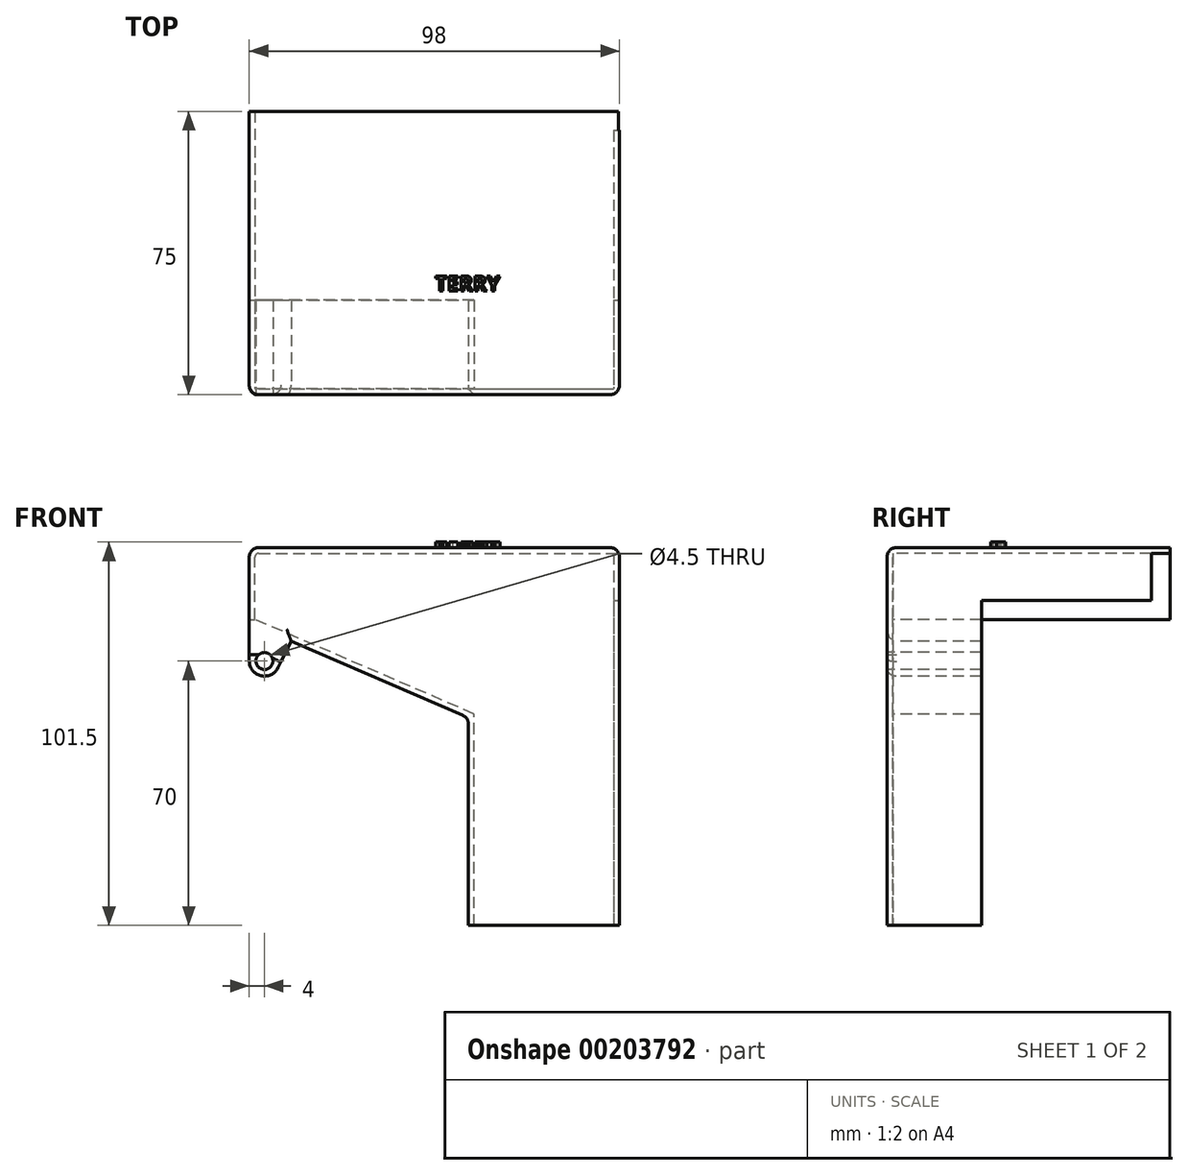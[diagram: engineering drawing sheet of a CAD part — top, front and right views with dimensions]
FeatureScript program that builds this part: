
annotation { "Feature Type Name" : "Feature", "Feature Type Description" : "" }
export const myFeature = defineFeature(function(context is Context, id is Id, definition is map)
    precondition{}
    {
        {
            var Q0;
            Q0=qCreatedBy(makeId("Front.planeOp"),FACE);
            var sketch = newSketch(context, id + "F0", { "sketchPlane" : qUnion([Q0])});
            skLineSegment(sketch, "E0", {"start": v(0, 0) * mm, "end": v(0, -55) * mm});
            skLineSegment(sketch, "E1", {"start": v(0, -55) * mm, "end": v(40, -55) * mm});
            skLineSegment(sketch, "E2", {"start": v(40, -55) * mm, "end": v(40, 45) * mm});
            skLineSegment(sketch, "E3", {"start": v(40, 45) * mm, "end": v(-58, 45) * mm});
            skLineSegment(sketch, "E4", {"start": v(-58, 45) * mm, "end": v(-58, 25) * mm});
            skLineSegment(sketch, "E5", {"start": v(-58, 25) * mm, "end": v(0, 0) * mm});
            skSolve(sketch);
        }
        {
            var Q0;
            Q0=makeQuery(id+"F0.imprint","IMPRINT",FACE,{"disambiguationData":[TD([[makeQuery(id+"F0.imprint","IMPRINT",EDGE,{"derivedFrom":sQuery(id+"F0.wireOp",EDGE,"E0")}),1.0]])]});
            extrude(context, id + "F1", {"entities" : qUnion([Q0]), "oppositeDirection" : true, "depth" : 1.5 * mm});
        }
        {
            var Q0;
            Q0=makeQuery(id+"F1.opExtrude","CAP_FACE",FACE,{"disambiguationData":[OSD([sQuery(id+"F0.wireOp",EDGE,"E0"),sQuery(id+"F0.wireOp",EDGE,"E1"),sQuery(id+"F0.wireOp",EDGE,"E2"),sQuery(id+"F0.wireOp",EDGE,"E3"),sQuery(id+"F0.wireOp",EDGE,"E4"),sQuery(id+"F0.wireOp",EDGE,"E5")])],"isStart":true});
            var sketch = newSketch(context, id + "F2", { "sketchPlane" : qUnion([Q0])});
            skLineSegment(sketch, "E6", {"start": v(-58, 25) * mm, "end": v(-58, 7.07) * mm, "construction": true});
            skLineSegment(sketch, "E7", {"start": v(-58, 25) * mm, "end": v(0, 0) * mm, "construction": true});
            skLineSegment(sketch, "E8.0", {"start": v(-54, 25) * mm, "end": v(-54, 7.07) * mm});
            skCircle(sketch, "E9", {"center": v(-54, 15) * mm, "radius": 2.25 * mm});
            skArc(sketch, "E10", {"start": v(-54, 19) * mm, "mid": v(-54.36, 18.98) * mm, "end": v(-54.71, 18.94) * mm});
            skLineSegment(sketch, "E11", {"start": v(-58, 15) * mm, "end": v(-58, 25) * mm});
            skLineSegment(sketch, "E12", {"start": v(-50.42, 13.21) * mm, "end": v(-46.92, 20.22) * mm});
            skLineSegment(sketch, "E13", {"start": v(-46.92, 20.22) * mm, "end": v(-58, 25) * mm});
            skArc(sketch, "E14.trimOffspring", {"start": v(-58, 15) * mm, "mid": v(-54.92, 11.1) * mm, "end": v(-50.42, 13.21) * mm});
            skSolve(sketch);
        }
        {
            var Q0;
            {var subQ10=sQuery(id+"F2.wireOp",EDGE,"E12");Q0=makeQuery(id+"F2.imprint","IMPRINT",FACE,{"disambiguationData":[TD([[makeQuery(id+"F2.imprint","IMPRINT",EDGE,{"derivedFrom":subQ10}),1.0]])]});}
            var Q1;
            {var subQ0=sQuery(id+"F2.wireOp",EDGE,"E14.trimOffspring");Q1=makeQuery(id+"F2.imprint","IMPRINT",FACE,{"disambiguationData":[TD([[makeQuery(id+"F2.imprint","IMPRINT",EDGE,{"derivedFrom":subQ0}),1.0]])]});}
            extrude(context, id + "F3", {"entities" : qUnion([Q0, Q1]), "operationType" : NewBodyOperationType.ADD, "oppositeDirection" : true, "depth" : 25 * mm});
        }
        {
            var Q0;
            Q0=makeQuery(id+"F1.opExtrude","CAP_FACE",FACE,{"disambiguationData":[OSD([sQuery(id+"F0.wireOp",EDGE,"E0"),sQuery(id+"F0.wireOp",EDGE,"E1"),sQuery(id+"F0.wireOp",EDGE,"E2"),sQuery(id+"F0.wireOp",EDGE,"E3"),sQuery(id+"F0.wireOp",EDGE,"E4"),sQuery(id+"F0.wireOp",EDGE,"E5")])],"isStart":false});
            var sketch = newSketch(context, id + "F4", { "sketchPlane" : qUnion([Q0])});
            skLineSegment(sketch, "E15", {"start": v(0, -55) * mm, "end": v(0, 0) * mm});
            skLineSegment(sketch, "E16", {"start": v(0, 0) * mm, "end": v(58, 25) * mm});
            skLineSegment(sketch, "E17", {"start": v(58, 25) * mm, "end": v(58, 45) * mm});
            skLineSegment(sketch, "E18", {"start": v(58, 45) * mm, "end": v(-40, 45) * mm});
            skLineSegment(sketch, "E19", {"start": v(-40, 45) * mm, "end": v(-40, -55) * mm});
            skLineSegment(sketch, "E20.0", {"start": v(-38.5, 43.5) * mm, "end": v(-38.5, -55) * mm});
            skLineSegment(sketch, "E20.1", {"start": v(-1.5, -55) * mm, "end": v(-1.5, 0.99) * mm});
            skLineSegment(sketch, "E20.2", {"start": v(-1.5, 0.99) * mm, "end": v(56.5, 25.99) * mm});
            skLineSegment(sketch, "E20.3", {"start": v(56.5, 25.99) * mm, "end": v(56.5, 43.5) * mm});
            skLineSegment(sketch, "E20.4", {"start": v(56.5, 43.5) * mm, "end": v(-38.5, 43.5) * mm});
            skSolve(sketch);
        }
        {
            var Q0;
            {var subQ2=sQuery(id+"F4.wireOp",EDGE,"E15");Q0=makeQuery(id+"F4.imprint","IMPRINT",FACE,{"disambiguationData":[TD([[makeQuery(id+"F4.imprint","IMPRINT",EDGE,{"derivedFrom":subQ2}),-1.0]])]});}
            extrude(context, id + "F5", {"entities" : qUnion([Q0]), "operationType" : NewBodyOperationType.ADD, "depth" : 23.5 * mm});
        }
        {
            var Q0;
            Q0=makeQuery(id+"F5.boolean.opBoolean","MERGE",FACE,{"derivedFrom":[makeQuery(id+"F3.opExtrude","CAP_FACE",FACE,{"disambiguationData":[OSD([sQuery(id+"F2.wireOp",EDGE,"E9"),sQuery(id+"F2.wireOp",EDGE,"E11"),sQuery(id+"F2.wireOp",EDGE,"E12"),sQuery(id+"F2.wireOp",EDGE,"E13"),sQuery(id+"F2.wireOp",EDGE,"E14.trimOffspring")])],"isStart":false}),makeQuery(id+"F5.opExtrude","CAP_FACE",FACE,{"disambiguationData":[OSD([sQuery(id+"F0.wireOp",EDGE,"E1"),sQuery(id+"F4.wireOp",EDGE,"E15"),sQuery(id+"F4.wireOp",EDGE,"E16"),sQuery(id+"F4.wireOp",EDGE,"E17"),sQuery(id+"F4.wireOp",EDGE,"E18"),sQuery(id+"F4.wireOp",EDGE,"E19"),sQuery(id+"F4.wireOp",EDGE,"E20.0"),sQuery(id+"F4.wireOp",EDGE,"E20.1"),sQuery(id+"F4.wireOp",EDGE,"E20.2"),sQuery(id+"F4.wireOp",EDGE,"E20.3"),sQuery(id+"F4.wireOp",EDGE,"E20.4")])],"isStart":false})]});
            var sketch = newSketch(context, id + "F6", { "sketchPlane" : qUnion([Q0])});
            skLineSegment(sketch, "E21", {"start": v(56.5, 25.99) * mm, "end": v(56.5, 43.5) * mm});
            skLineSegment(sketch, "E22", {"start": v(56.5, 43.5) * mm, "end": v(-40, 43.5) * mm});
            skLineSegment(sketch, "E23", {"start": v(-40, 43.5) * mm, "end": v(-40, 45) * mm});
            skLineSegment(sketch, "E24", {"start": v(-40, 45) * mm, "end": v(58, 45) * mm});
            skLineSegment(sketch, "E25", {"start": v(58, 45) * mm, "end": v(58, 25.99) * mm});
            skLineSegment(sketch, "E26", {"start": v(58, 25.99) * mm, "end": v(56.5, 25.99) * mm});
            skSolve(sketch);
        }
        {
            var Q0;
            {var subQ3=sQuery(id+"F6.wireOp",EDGE,"E21");Q0=makeQuery(id+"F6.imprint","IMPRINT",FACE,{"disambiguationData":[TD([[makeQuery(id+"F6.imprint","IMPRINT",EDGE,{"derivedFrom":subQ3}),-1.0]])]});}
            extrude(context, id + "F7", {"entities" : qUnion([Q0]), "operationType" : NewBodyOperationType.ADD, "depth" : 50 * mm});
        }
        {
            var Q0;
            {var subQ0=sQuery(id+"F4.wireOp",EDGE,"E20.0");var subQ1=sQuery(id+"F0.wireOp",EDGE,"E1");var subQ2=sQuery(id+"F4.wireOp",EDGE,"E19");var subQ3=sQuery(id+"F4.wireOp",EDGE,"E20.4");var subQ4=sQuery(id+"F4.wireOp",EDGE,"E15");var subQ6=sQuery(id+"F4.wireOp",EDGE,"E20.1");Q0=makeQuery(id+"F7.boolean.opBoolean","SPLIT",FACE,{"disambiguationData":[TD([makeQuery(id+"F1.opExtrude","SWEPT_FACE",FACE,{"disambiguationData":[OSD([sQuery(id+"F0.wireOp",EDGE,"E2")])]})])],"derivedFrom":makeQuery(id+"F5.boolean.opBoolean","MERGE",FACE,{"derivedFrom":[makeQuery(id+"F3.opExtrude","CAP_FACE",FACE,{"disambiguationData":[OSD([sQuery(id+"F2.wireOp",EDGE,"E9"),sQuery(id+"F2.wireOp",EDGE,"E11"),sQuery(id+"F2.wireOp",EDGE,"E12"),sQuery(id+"F2.wireOp",EDGE,"E13"),sQuery(id+"F2.wireOp",EDGE,"E14.trimOffspring")])],"isStart":false}),makeQuery(id+"F5.opExtrude","CAP_FACE",FACE,{"disambiguationData":[OSD([subQ1,subQ4,sQuery(id+"F4.wireOp",EDGE,"E16"),sQuery(id+"F4.wireOp",EDGE,"E17"),sQuery(id+"F4.wireOp",EDGE,"E18"),subQ2,subQ0,subQ6,sQuery(id+"F4.wireOp",EDGE,"E20.2"),sQuery(id+"F4.wireOp",EDGE,"E20.3"),subQ3])],"isStart":false})]})});}
            var sketch = newSketch(context, id + "F8", { "sketchPlane" : qUnion([Q0])});
            skLineSegment(sketch, "E27", {"start": v(-40, 43.5) * mm, "end": v(-38.5, 43.5) * mm});
            skLineSegment(sketch, "E28", {"start": v(-38.5, 43.5) * mm, "end": v(-38.5, 31) * mm});
            skLineSegment(sketch, "E29", {"start": v(-38.5, 31) * mm, "end": v(-40, 31) * mm});
            skLineSegment(sketch, "E30", {"start": v(-40, 31) * mm, "end": v(-40, 43.5) * mm});
            skSolve(sketch);
        }
        {
            var Q0;
            Q0=makeQuery(id+"F8.imprint","IMPRINT",FACE,{"disambiguationData":[TD([[makeQuery(id+"F8.imprint","IMPRINT",EDGE,{"derivedFrom":sQuery(id+"F8.wireOp",EDGE,"E27")}),1.0]])]});
            extrude(context, id + "F9", {"entities" : qUnion([Q0]), "operationType" : NewBodyOperationType.ADD, "depth" : 45 * mm});
        }
        {
            var Q0;
            Q0=makeQuery(id+"F7.boolean.opBoolean","MERGE",FACE,{"derivedFrom":[makeQuery(id+"F5.boolean.opBoolean","MERGE",FACE,{"derivedFrom":[makeQuery(id+"F1.opExtrude","SWEPT_FACE",FACE,{"disambiguationData":[OSD([sQuery(id+"F0.wireOp",EDGE,"E3")])]}),makeQuery(id+"F5.opExtrude","SWEPT_FACE",FACE,{"disambiguationData":[OSD([sQuery(id+"F4.wireOp",EDGE,"E18")])]})]}),makeQuery(id+"F7.opExtrude","SWEPT_FACE",FACE,{"disambiguationData":[OSD([sQuery(id+"F6.wireOp",EDGE,"E24")])]})]});
            var sketch = newSketch(context, id + "F10", { "sketchPlane" : qUnion([Q0])});
            skText(sketch, "E31", { "text": "TERRY", "fontName": "OpenSans-Bold.ttf"});
            const initialGuessF10  = {"E31": [-0.00878, 0.02744, 1, 0, 0.004]};
            skSetInitialGuess(sketch, initialGuessF10);
            skSolve(sketch);
        }
        {
            var Q0;
            Q0 = qSketchRegion(id + "F10", true);
            extrude(context, id + "F11", {"entities" : qUnion([Q0]), "operationType" : NewBodyOperationType.ADD, "depth" : 1.5 * mm});
        }
        {
            var Q0;
            Q0=makeQuery(id+"F5.opExtrude","CAP_EDGE",EDGE,{"disambiguationData":[OSD([sQuery(id+"F4.wireOp",EDGE,"E20.1")])],"isStart":true});
            var Q1;
            Q1=makeQuery(id+"F5.opExtrude","CAP_EDGE",EDGE,{"disambiguationData":[OSD([sQuery(id+"F4.wireOp",EDGE,"E20.2")])],"isStart":true});
            var Q2;
            Q2=makeQuery(id+"F5.opExtrude","CAP_EDGE",EDGE,{"disambiguationData":[OSD([sQuery(id+"F4.wireOp",EDGE,"E20.3")])],"isStart":true});
            var Q3;
            Q3=makeQuery(id+"F7.boolean.opBoolean","MERGE",EDGE,{"derivedFrom":[makeQuery(id+"F5.opExtrude","SWEPT_EDGE",EDGE,{"disambiguationData":[OSD([sQuery(id+"F4.wireOp",EDGE,"E20.3"),sQuery(id+"F4.wireOp",EDGE,"E20.4")])]}),makeQuery(id+"F7.opExtrude","SWEPT_EDGE",EDGE,{"disambiguationData":[OSD([sQuery(id+"F6.wireOp",EDGE,"E21"),sQuery(id+"F6.wireOp",EDGE,"E22")])]})]});
            var Q4;
            Q4=makeQuery(id+"F5.opExtrude","CAP_EDGE",EDGE,{"disambiguationData":[OSD([sQuery(id+"F4.wireOp",EDGE,"E20.4")])],"isStart":true});
            var Q5;
            Q5=makeQuery(id+"F9.boolean.opBoolean","MERGE",EDGE,{"derivedFrom":[makeQuery(id+"F5.opExtrude","SWEPT_EDGE",EDGE,{"disambiguationData":[OSD([sQuery(id+"F4.wireOp",EDGE,"E20.0"),sQuery(id+"F4.wireOp",EDGE,"E20.4")])]}),makeQuery(id+"F9.opExtrude","SWEPT_EDGE",EDGE,{"disambiguationData":[OSD([sQuery(id+"F8.wireOp",EDGE,"E27"),sQuery(id+"F8.wireOp",EDGE,"E28")])]})]});
            var Q6;
            Q6=makeQuery(id+"F5.opExtrude","CAP_EDGE",EDGE,{"disambiguationData":[OSD([sQuery(id+"F4.wireOp",EDGE,"E20.0")])],"isStart":true});
            fillet(context, id + "F12", {"entities" : qUnion([Q0, Q1, Q2, Q3, Q4, Q5, Q6]), "radius" : 1 * mm, "tangentPropagation" : true, "allowEdgeOverflow" : false});
        }
        {
            var Q0;
            Q0=makeQuery(id+"F7.boolean.opBoolean","MERGE",EDGE,{"derivedFrom":[makeQuery(id+"F5.boolean.opBoolean","MERGE",EDGE,{"derivedFrom":[makeQuery(id+"F1.opExtrude","SWEPT_EDGE",EDGE,{"disambiguationData":[OSD([sQuery(id+"F0.wireOp",EDGE,"E3"),sQuery(id+"F0.wireOp",EDGE,"E4")])]}),makeQuery(id+"F5.opExtrude","SWEPT_EDGE",EDGE,{"disambiguationData":[OSD([sQuery(id+"F4.wireOp",EDGE,"E17"),sQuery(id+"F4.wireOp",EDGE,"E18")])]})]}),makeQuery(id+"F7.opExtrude","SWEPT_EDGE",EDGE,{"disambiguationData":[OSD([sQuery(id+"F6.wireOp",EDGE,"E24"),sQuery(id+"F6.wireOp",EDGE,"E25")])]})]});
            var Q1;
            Q1=makeQuery(id+"F1.opExtrude","CAP_EDGE",EDGE,{"disambiguationData":[OSD([sQuery(id+"F0.wireOp",EDGE,"E3")])],"isStart":true});
            var Q2;
            Q2=makeQuery(id+"F7.boolean.opBoolean","MERGE",EDGE,{"derivedFrom":[makeQuery(id+"F5.boolean.opBoolean","MERGE",EDGE,{"derivedFrom":[makeQuery(id+"F1.opExtrude","SWEPT_EDGE",EDGE,{"disambiguationData":[OSD([sQuery(id+"F0.wireOp",EDGE,"E2"),sQuery(id+"F0.wireOp",EDGE,"E3")])]}),makeQuery(id+"F5.opExtrude","SWEPT_EDGE",EDGE,{"disambiguationData":[OSD([sQuery(id+"F4.wireOp",EDGE,"E18"),sQuery(id+"F4.wireOp",EDGE,"E19")])]})]}),makeQuery(id+"F7.opExtrude","SWEPT_EDGE",EDGE,{"disambiguationData":[OSD([sQuery(id+"F6.wireOp",EDGE,"E23"),sQuery(id+"F6.wireOp",EDGE,"E24")])]})]});
            var Q3;
            Q3=makeQuery(id+"F1.opExtrude","CAP_EDGE",EDGE,{"disambiguationData":[OSD([sQuery(id+"F0.wireOp",EDGE,"E2")])],"isStart":true});
            var Q4;
            Q4=makeQuery(id+"F1.opExtrude","CAP_EDGE",EDGE,{"disambiguationData":[OSD([sQuery(id+"F0.wireOp",EDGE,"E0")])],"isStart":true});
            var Q5;
            Q5=makeQuery(id+"F1.opExtrude","CAP_EDGE",EDGE,{"disambiguationData":[OSD([sQuery(id+"F0.wireOp",EDGE,"E5")])],"isStart":true});
            var Q6;
            Q6=makeQuery(id+"F3.boolean.opBoolean","MERGE",EDGE,{"derivedFrom":[makeQuery(id+"F1.opExtrude","CAP_EDGE",EDGE,{"disambiguationData":[OSD([sQuery(id+"F0.wireOp",EDGE,"E4")])],"isStart":true}),makeQuery(id+"F3.opExtrude","CAP_EDGE",EDGE,{"disambiguationData":[OSD([sQuery(id+"F2.wireOp",EDGE,"E11")])],"isStart":true})]});
            var Q7;
            Q7=makeQuery(id+"F5.boolean.opBoolean","MERGE",EDGE,{"derivedFrom":[makeQuery(id+"F1.opExtrude","SWEPT_EDGE",EDGE,{"disambiguationData":[OSD([sQuery(id+"F0.wireOp",EDGE,"E0"),sQuery(id+"F0.wireOp",EDGE,"E5")])]}),makeQuery(id+"F5.opExtrude","SWEPT_EDGE",EDGE,{"disambiguationData":[OSD([sQuery(id+"F4.wireOp",EDGE,"E15"),sQuery(id+"F4.wireOp",EDGE,"E16")])]})]});
            fillet(context, id + "F13", {"entities" : qUnion([Q0, Q1, Q2, Q3, Q4, Q5, Q6, Q7]), "radius" : 2.5 * mm, "tangentPropagation" : true, "allowEdgeOverflow" : false});
        }
    });
